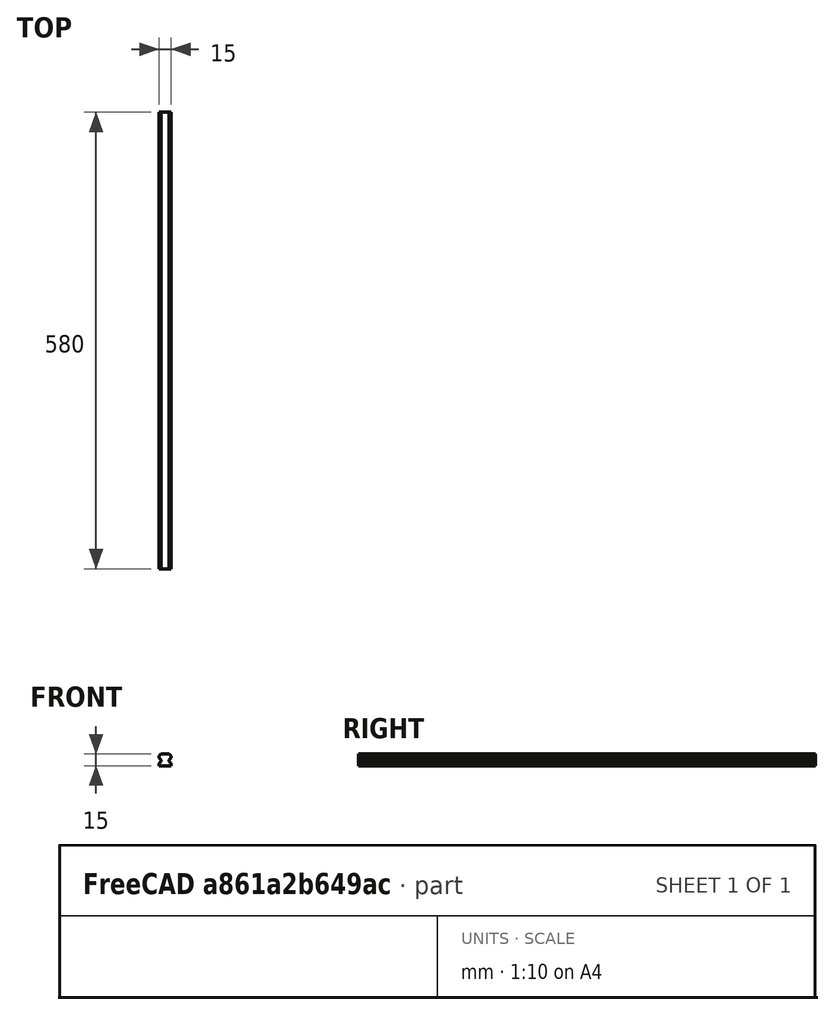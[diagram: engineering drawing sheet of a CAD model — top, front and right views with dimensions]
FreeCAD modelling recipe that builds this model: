
FCSTD DOCUMENT  (FreeCAD 0.19R)
Label: y_rail
License: All rights reserved
LicenseURL: http://en.wikipedia.org/wiki/All_rights_reserved
objects: PartDesign::CoordinateSystem×2, Sketcher::SketchObject×1, PartDesign::Pad×1, PartDesign::Body×1
note: 6 computed .brp shape members not serialized (recipe doc carries the construction recipe); baked Part::Feature solids carry a one-line shape summary decoded from their .brp

FEATURE [Sketcher::SketchObject] Sketch
  FullyConstrained = true
  MapMode = 5
  Placement = pos=(0,0,0) rot=(1,0,0;1.5708rad)
  Support = -> [XZ_Plane]
  sketch-geometry (14):
    g0: LineSegment StartX=-7.5 StartY=0 StartZ=0 EndX=7.5 EndY=0 EndZ=0
    g1: LineSegment StartX=-7.5 StartY=0 StartZ=0 EndX=-7.5 EndY=2.7 EndZ=0
    g2: LineSegment StartX=7.5 StartY=0 StartZ=0 EndX=7.5 EndY=2.7 EndZ=0
    g3: LineSegment StartX=-7.5 StartY=2.7 StartZ=0 EndX=-5 EndY=5.2 EndZ=0
    g4: LineSegment StartX=-5 StartY=5.2 StartZ=0 EndX=-5 EndY=7.2 EndZ=0
    g5: LineSegment StartX=-5 StartY=7.2 StartZ=0 EndX=-7.5 EndY=9.7 EndZ=0
    g6: LineSegment StartX=-7.5 StartY=9.7 StartZ=0 EndX=-7.5 EndY=12.5 EndZ=0
    g7: LineSegment StartX=-7.5 StartY=12.5 StartZ=0 EndX=-5 EndY=15 EndZ=0
    g8: LineSegment StartX=-5 StartY=15 StartZ=0 EndX=5 EndY=15 EndZ=0
    g9: LineSegment StartX=5 StartY=15 StartZ=0 EndX=7.5 EndY=12.5 EndZ=0
    g10: LineSegment StartX=7.5 StartY=12.5 StartZ=0 EndX=7.5 EndY=9.7 EndZ=0
    g11: LineSegment StartX=7.5 StartY=9.7 StartZ=0 EndX=5 EndY=7.2 EndZ=0
    g12: LineSegment StartX=5 StartY=7.2 StartZ=0 EndX=5 EndY=5.2 EndZ=0
    g13: LineSegment StartX=7.5 StartY=2.7 StartZ=0 EndX=5 EndY=5.2 EndZ=0
  constraints (36):
    c: PointOnObject(g0,g-1)
    c: Coincident(g1,g0)
    c: Vertical(g1)
    c: Coincident(g2,g0)
    c: Vertical(g2)
    c: Coincident(g3,g1)
    c: Coincident(g4,g3)
    c: Vertical(g4)
    c: Coincident(g5,g4)
    c: Coincident(g6,g5)
    c: Coincident(g7,g6)
    c: Coincident(g8,g7)
    c: Coincident(g9,g8)
    c: Coincident(g10,g9)
    c: Coincident(g11,g10)
    c: Coincident(g12,g11)
    c: Coincident(g13,g2)
    c: Coincident(g13,g12)
    c: Symmetric(g0,g0,g-2)
    c: DistanceX(g0,g0) = 15
    c: DistanceY(g0,g8) = 15
    c: DistanceX(g8,g8) = 10
    c: Symmetric(g7,g8,g-2)
    c: Vertical(g6)
    c: Symmetric(g9,g6,g-2)
    c: Symmetric(g5,g10,g-2)
    c: Symmetric(g4,g11,g-2)
    c: Symmetric(g12,g3,g-2)
    c: DistanceX(g8,g9) = 2.5
    c: DistanceY(g9,g8) = 2.5
    c: DistanceY(g11,g10) = 2.5
    c: DistanceY(g13,g13) = 2.5
    c: DistanceY(g12,g12) = 2
    c: DistanceY(g10,g10) = 2.8
    c: DistanceX(g11,g11) = 2.5
    c: Equal(g2,g1)
FEATURE [PartDesign::Pad] Pad
  Direction = (1,1,1)
  Length = 580
  Length2 = 100
  Placement = pos=(0,0,0) rot=(1,0,0;1.5708rad)
  Profile = -> Sketch
  Type = 0
FEATURE [PartDesign::CoordinateSystem] LCS_mount
  AttacherType = Attacher::AttachEngine3D
  MapMode = 5
  Placement = pos=(0,0,0) rot=(1,0,0;3.14159rad)
  Support = -> [Pad]
FEATURE [PartDesign::CoordinateSystem] LCS_caret_mount
  AttacherType = Attacher::AttachEngine3D
  AttachmentOffset = pos=(0,100,0) rot=(0,0,1;0rad)
  MapMode = 5
  Placement = pos=(0,-100,15) rot=(0,0,1;3.14159rad)
  Support = -> [Pad]
FEATURE [PartDesign::Body] Body
  Group = -> [Sketch,Pad,LCS_mount,LCS_caret_mount]
  Origin = -> Origin
  Tip = -> Pad
